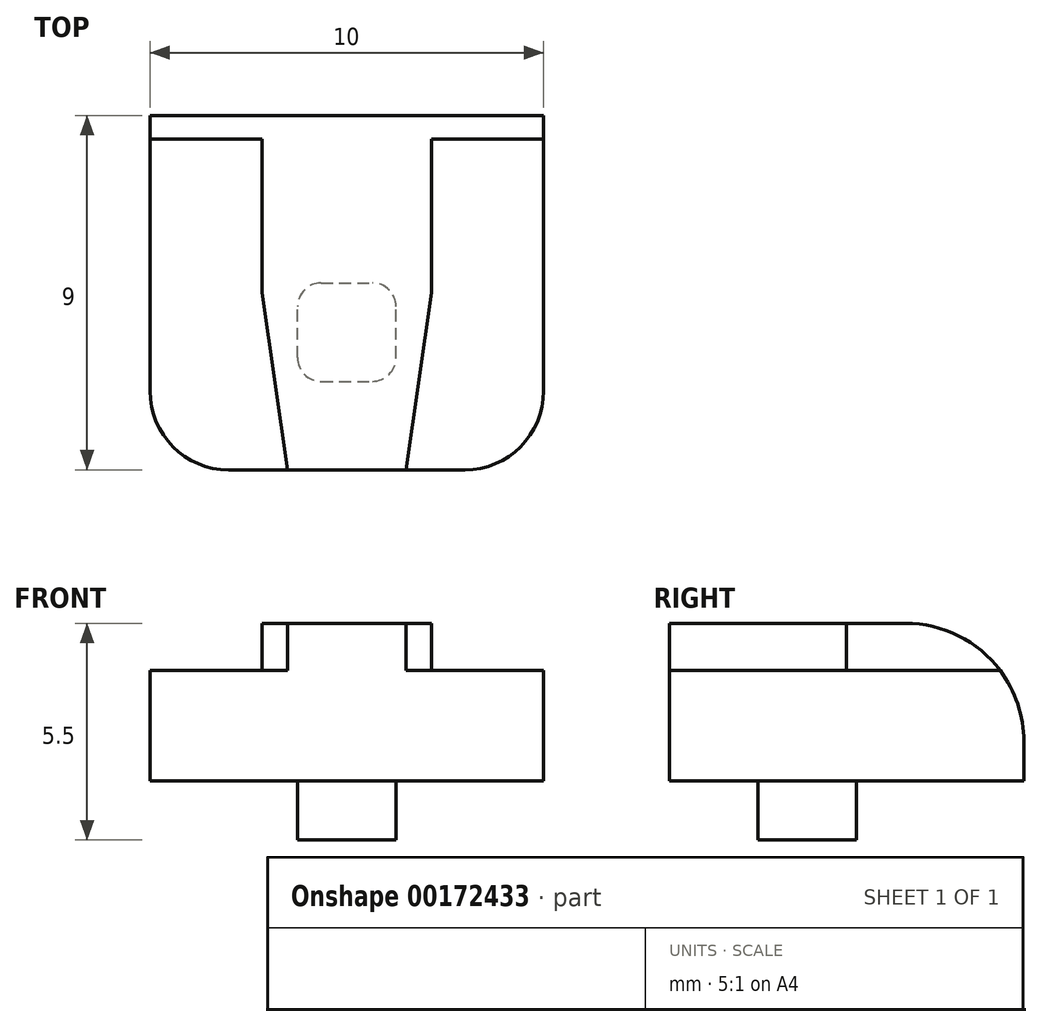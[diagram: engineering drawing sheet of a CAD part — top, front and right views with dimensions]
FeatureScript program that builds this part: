
annotation { "Feature Type Name" : "Feature", "Feature Type Description" : "" }
export const myFeature = defineFeature(function(context is Context, id is Id, definition is map)
    precondition{}
    {
        {
            var Q0;
            Q0=qCreatedBy(makeId("Top.planeOp"),FACE);
            var sketch = newSketch(context, id + "F0", { "sketchPlane" : qUnion([Q0])});
            skLineSegment(sketch, "E0.bottom", {"start": v(-5, 4.5) * mm, "end": v(5, 4.5) * mm});
            skLineSegment(sketch, "E0.top", {"start": v(-5, -4.5) * mm, "end": v(5, -4.5) * mm});
            skLineSegment(sketch, "E0.left", {"start": v(-5, 4.5) * mm, "end": v(-5, -4.5) * mm});
            skLineSegment(sketch, "E0.right", {"start": v(5, 4.5) * mm, "end": v(5, -4.5) * mm});
            skPoint(sketch, "E0.middle", {"position": v(0, 0) * mm});
            skSolve(sketch);
        }
        {
            var Q0;
            Q0=makeQuery(id+"F0.imprint","IMPRINT",FACE,{"disambiguationData":[TD([[makeQuery(id+"F0.imprint","IMPRINT",EDGE,{"derivedFrom":sQuery(id+"F0.wireOp",EDGE,"E0.bottom")}),-1.0]])]});
            extrude(context, id + "F1", {"entities" : qUnion([Q0]), "depth" : 2.8 * mm});
        }
        {
            var Q0;
            Q0=makeQuery(id+"F1.opExtrude","CAP_FACE",FACE,{"disambiguationData":[OSD([sQuery(id+"F0.wireOp",EDGE,"E0.bottom"),sQuery(id+"F0.wireOp",EDGE,"E0.top"),sQuery(id+"F0.wireOp",EDGE,"E0.left"),sQuery(id+"F0.wireOp",EDGE,"E0.right")])],"isStart":false});
            var sketch = newSketch(context, id + "F2", { "sketchPlane" : qUnion([Q0])});
            skLineSegment(sketch, "E1", {"start": v(-2.15, 4.5) * mm, "end": v(-2.15, 0) * mm});
            skLineSegment(sketch, "E2", {"start": v(-2.15, 0) * mm, "end": v(-1.5, -4.5) * mm});
            skLineSegment(sketch, "E3.MirrorCS", {"start": v(2.15, 0) * mm, "end": v(1.5, -4.5) * mm});
            skLineSegment(sketch, "E4.MirrorCS", {"start": v(2.15, 4.5) * mm, "end": v(2.15, 0) * mm});
            skSolve(sketch);
        }
        {
            var Q0;
            {var subQ0=sQuery(id+"F2.wireOp",EDGE,"E1");Q0=makeQuery(id+"F2.imprint","IMPRINT",FACE,{"disambiguationData":[TD([[makeQuery(id+"F2.imprint","IMPRINT",EDGE,{"derivedFrom":subQ0}),1.0]])]});}
            extrude(context, id + "F3", {"entities" : qUnion([Q0]), "operationType" : NewBodyOperationType.ADD, "depth" : 1.2 * mm});
        }
        {
            var Q0;
            Q0=makeQuery(id+"F1.opExtrude","CAP_FACE",FACE,{"disambiguationData":[OSD([sQuery(id+"F0.wireOp",EDGE,"E0.bottom"),sQuery(id+"F0.wireOp",EDGE,"E0.top"),sQuery(id+"F0.wireOp",EDGE,"E0.left"),sQuery(id+"F0.wireOp",EDGE,"E0.right")])],"isStart":true});
            var sketch = newSketch(context, id + "F4", { "sketchPlane" : qUnion([Q0])});
            skLineSegment(sketch, "E5.bottom", {"start": v(-1.25, 2.25) * mm, "end": v(1.25, 2.25) * mm});
            skLineSegment(sketch, "E5.top", {"start": v(-1.25, -0.25) * mm, "end": v(1.25, -0.25) * mm});
            skLineSegment(sketch, "E5.left", {"start": v(-1.25, 2.25) * mm, "end": v(-1.25, -0.25) * mm});
            skLineSegment(sketch, "E5.right", {"start": v(1.25, 2.25) * mm, "end": v(1.25, -0.25) * mm});
            skPoint(sketch, "E5.middle", {"position": v(0, 1) * mm});
            skSolve(sketch);
        }
        {
            var Q0;
            Q0=makeQuery(id+"F4.imprint","IMPRINT",FACE,{"disambiguationData":[TD([[makeQuery(id+"F4.imprint","IMPRINT",EDGE,{"derivedFrom":sQuery(id+"F4.wireOp",EDGE,"E5.bottom")}),-1.0]])]});
            extrude(context, id + "F5", {"entities" : qUnion([Q0]), "operationType" : NewBodyOperationType.ADD, "depth" : 1.5 * mm});
        }
        {
            var Q0;
            Q0=makeQuery(id+"F1.opExtrude","SWEPT_EDGE",EDGE,{"disambiguationData":[OSD([sQuery(id+"F0.wireOp",EDGE,"E0.top"),sQuery(id+"F0.wireOp",EDGE,"E0.right")])]});
            var Q1;
            Q1=makeQuery(id+"F1.opExtrude","SWEPT_EDGE",EDGE,{"disambiguationData":[OSD([sQuery(id+"F0.wireOp",EDGE,"E0.top"),sQuery(id+"F0.wireOp",EDGE,"E0.left")])]});
            fillet(context, id + "F6", {"entities" : qUnion([Q0, Q1]), "radius" : 2 * mm, "tangentPropagation" : true, "allowEdgeOverflow" : false});
        }
        {
            var Q0;
            Q0=makeQuery(id+"F3.opExtrude","CAP_EDGE",EDGE,{"disambiguationData":[OSD([sQuery(id+"F0.wireOp",EDGE,"E0.bottom")])],"isStart":false});
            fillet(context, id + "F7", {"entities" : qUnion([Q0]), "radius" : 3 * mm, "tangentPropagation" : true, "allowEdgeOverflow" : false});
        }
        {
            var Q0;
            Q0=makeQuery(id+"F5.opExtrude","SWEPT_EDGE",EDGE,{"disambiguationData":[OSD([sQuery(id+"F4.wireOp",EDGE,"E5.bottom"),sQuery(id+"F4.wireOp",EDGE,"E5.right")])]});
            var Q1;
            Q1=makeQuery(id+"F5.opExtrude","SWEPT_EDGE",EDGE,{"disambiguationData":[OSD([sQuery(id+"F4.wireOp",EDGE,"E5.bottom"),sQuery(id+"F4.wireOp",EDGE,"E5.left")])]});
            var Q2;
            Q2=makeQuery(id+"F5.opExtrude","SWEPT_EDGE",EDGE,{"disambiguationData":[OSD([sQuery(id+"F4.wireOp",EDGE,"E5.top"),sQuery(id+"F4.wireOp",EDGE,"E5.right")])]});
            var Q3;
            Q3=makeQuery(id+"F5.opExtrude","SWEPT_EDGE",EDGE,{"disambiguationData":[OSD([sQuery(id+"F4.wireOp",EDGE,"E5.top"),sQuery(id+"F4.wireOp",EDGE,"E5.left")])]});
            fillet(context, id + "F8", {"entities" : qUnion([Q0, Q1, Q2, Q3]), "radius" : 0.6 * mm, "tangentPropagation" : true, "allowEdgeOverflow" : false});
        }
    });
